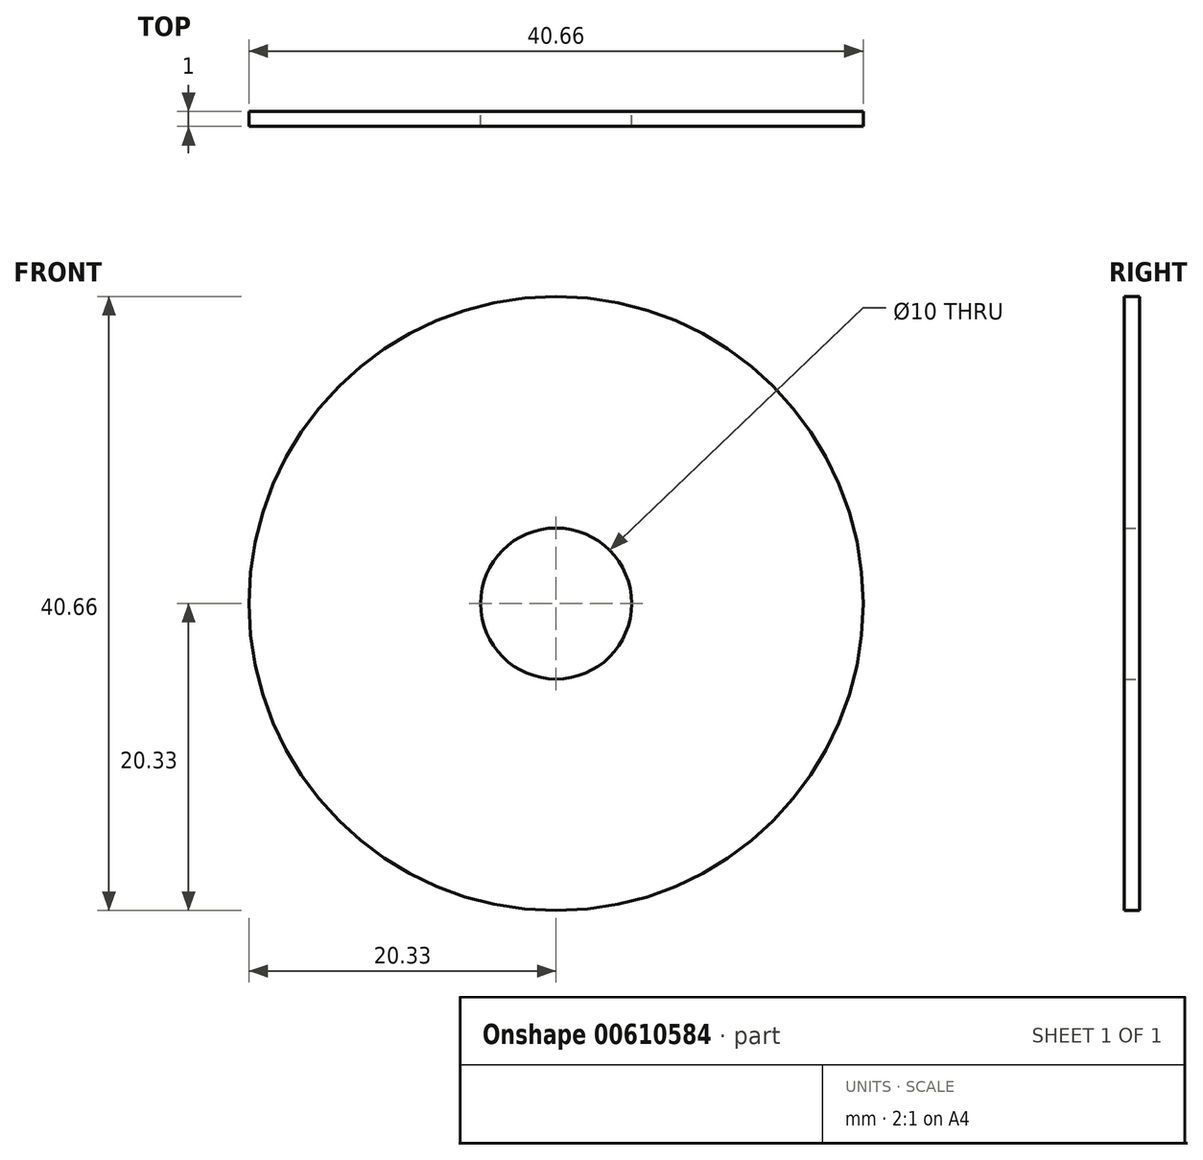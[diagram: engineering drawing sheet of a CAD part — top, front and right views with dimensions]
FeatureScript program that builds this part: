
annotation { "Feature Type Name" : "Feature", "Feature Type Description" : "" }
export const myFeature = defineFeature(function(context is Context, id is Id, definition is map)
    precondition{}
    {
        {
            var Q0;
            Q0=qCreatedBy(makeId("Front.planeOp"),FACE);
            var sketch = newSketch(context, id + "F0", { "sketchPlane" : qUnion([Q0])});
            skCircle(sketch, "E0", {"center": v(0, 0) * mm, "radius": 20.33 * mm});
            skCircle(sketch, "E1", {"center": v(0, 0) * mm, "radius": 5 * mm});
            skSolve(sketch);
        }
        {
            var Q0;
            Q0=makeQuery(id+"F0.imprint","IMPRINT",FACE,{"disambiguationData":[TD([[makeQuery(id+"F0.imprint","IMPRINT",EDGE,{"derivedFrom":sQuery(id+"F0.wireOp",EDGE,"E0")}),1.0]])]});
            extrude(context, id + "F1", {"entities" : qUnion([Q0]), "depth" : 1 * mm, "offsetDistance" : 25 * mm});
        }
    });
